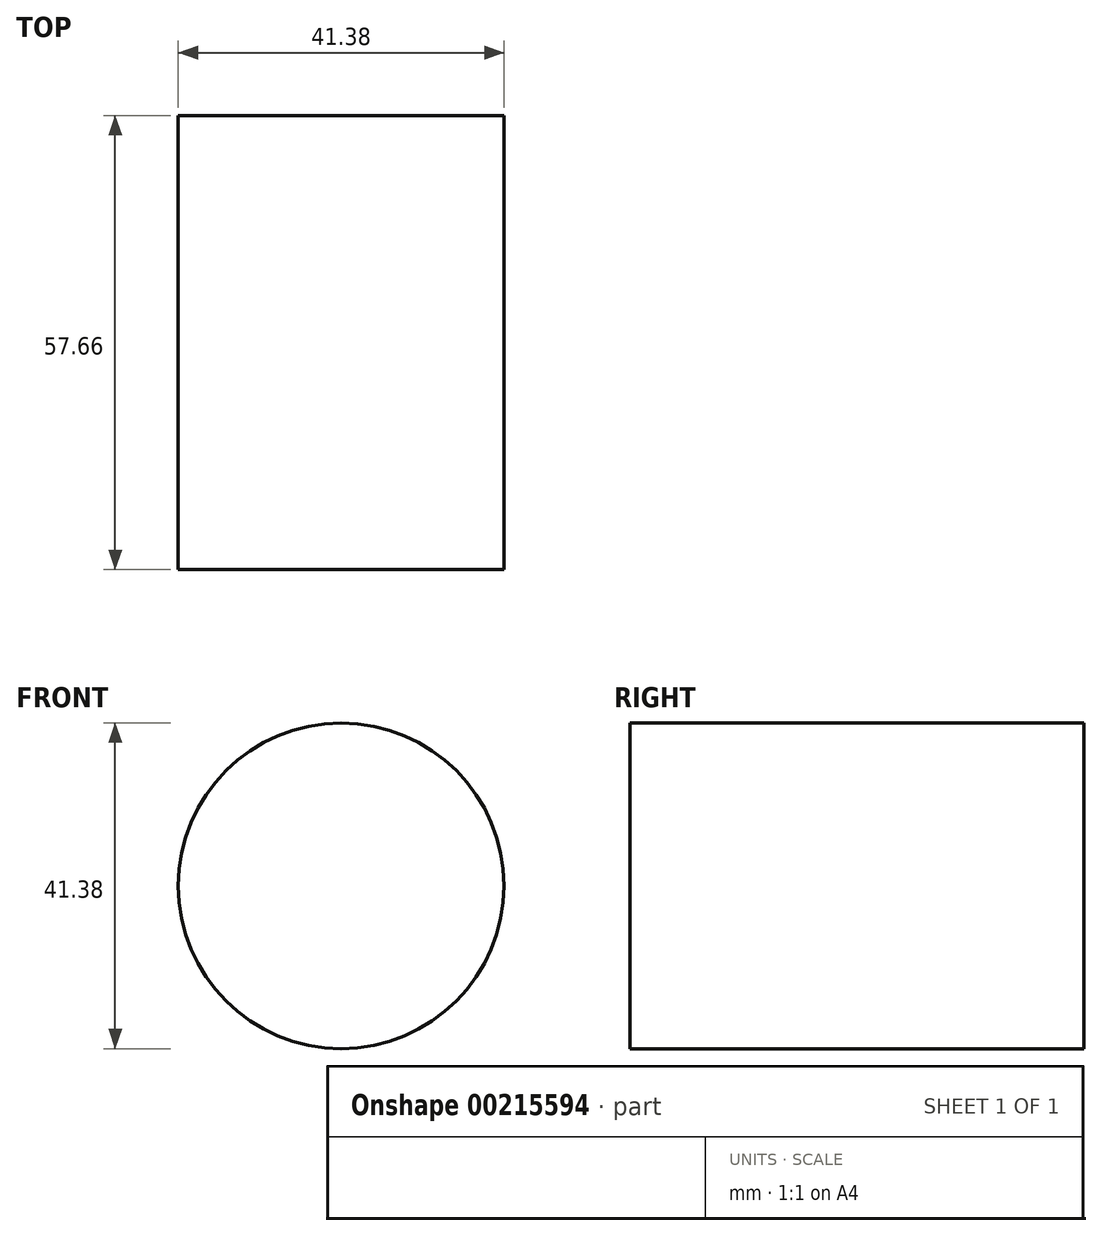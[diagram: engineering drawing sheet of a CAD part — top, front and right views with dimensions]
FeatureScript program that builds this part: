
annotation { "Feature Type Name" : "Feature", "Feature Type Description" : "" }
export const myFeature = defineFeature(function(context is Context, id is Id, definition is map)
    precondition{}
    {
        {
            var Q0;
            Q0=qCreatedBy(makeId("Front.planeOp"),FACE);
            var sketch = newSketch(context, id + "F0", { "sketchPlane" : qUnion([Q0])});
            skCircle(sketch, "E0", {"center": v(-36.18, 0) * mm, "radius": 20.7 * mm});
            skArc(sketch, "E1", {"start": v(-61.51, 22.27) * mm, "mid": v(-46.44, 26.28) * mm, "end": v(-40.78, 40.82) * mm});
            skSolve(sketch);
        }
        {
            var Q0;
            Q0 = qSketchRegion(id + "F0", true);
            extrude(context, id + "F1", {"entities" : qUnion([Q0]), "oppositeDirection" : true, "depth" : 57.66 * mm});
        }
        {
            var Q0;
            Q0=qCreatedBy(makeId("Right.planeOp"),FACE);
            var sketch = newSketch(context, id + "F2", { "sketchPlane" : qUnion([Q0])});
            skArc(sketch, "E2", {"start": v(57.9, 27.65) * mm, "mid": v(-0.58, 46.25) * mm, "end": v(-57.9, 24.32) * mm});
            skSolve(sketch);
        }
    });
